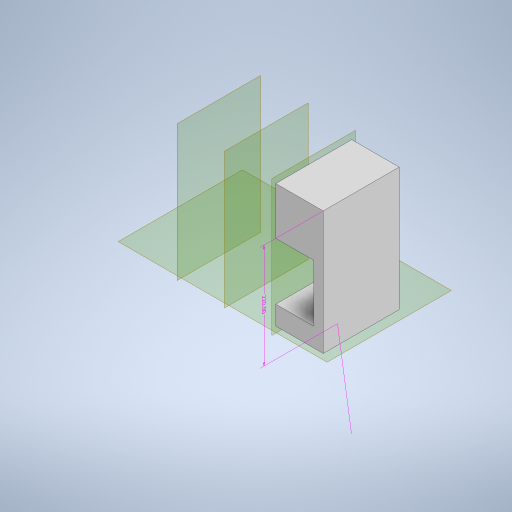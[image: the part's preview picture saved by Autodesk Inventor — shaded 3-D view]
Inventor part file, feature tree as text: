
AUTODESK INVENTOR PART (.ipt)
format: ipt  version: 2023 (Build 270158000, 158)  size: 323,584 bytes
history: native  units: mm
features: extrude x6, plane x6, sketch x6, other x5, split x2
ambient origin geometry x8: Origin, YZ Plane, XZ Plane, XY Plane, X Axis, Y Axis, Z Axis, Center Point
bodies: Body1 (feature_tree), Body2 (feature_tree)
feature tree (25):
  other  "Sólido1"
  other  "Anotaciones"
  extrude  "Extrusión1"  Depth=80.0mm
  extrude  "Extrusión2"  Depth=130.0mm
  extrude  "Extrusión3"  Depth=20.0mm
  extrude  "Extrusión4"  Depth=60.0mm
  plane  "Plano de trabajo1"
  extrude  "Extrusión6"  Depth=20.0mm
  plane  "Plano de trabajo3"
  extrude  "Extrusión7"  [1 undecoded]
  plane  "Plano de trabajo4"
  split  "Dividir1"
  other  "Suprimir cara4"
  plane  "Plano de trabajo5"
  plane  "Plano de trabajo6"
  plane  "Plano de trabajo7"
  split  "Dividir2"
  sketch  "Boceto1"  dims[d0=200.0mm d1=80.0mm]
  sketch  "Boceto2"  dims[d2=130.0mm d3=0.0mm d4=180.0mm]
  sketch  "Boceto3"  dims[d5=60.0mm d6=20.0mm]
  sketch  "Boceto4"  dims[d7=60.0mm d8=0.0mm d9=21.0mm d10=43.0mm]
  sketch  "Boceto7"  dims[d11=43.0mm d12=0.0mm d13=20.0mm]
  other  "Sólido3"
  sketch  "Boceto10"  dims[d14=90.0mm d15=0.0mm d16=-90.0mm d28=20.0mm d29=20.0mm d30=30.0mm d31=30.0mm d32=20.0mm d33=35.0mm d34=35.0mm d35=69.0mm d36=10.0mm d37=0.0mm d45=1.5mm d50=10.0mm d51=0.0mm d52=10.0mm d53=89.5mm d54=90.0deg d38=3.166395mm d39=4.283575mm d40=220.0mm]
  other  "Cota lineal 1"
note: 1 required parameter value undecoded (feature->parameter linkage not recoverable at this tier; creation-order binding heuristic only, values carry confidence <= 0.55)
